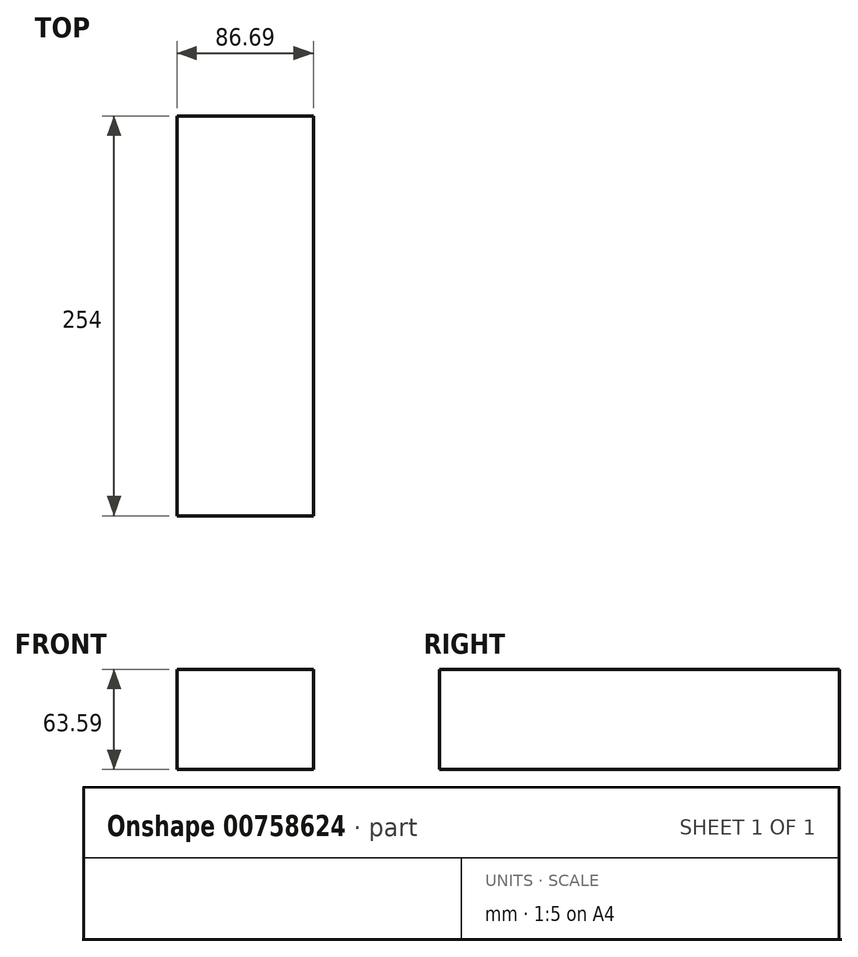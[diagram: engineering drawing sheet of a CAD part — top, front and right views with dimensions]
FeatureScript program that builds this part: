
annotation { "Feature Type Name" : "Feature", "Feature Type Description" : "" }
export const myFeature = defineFeature(function(context is Context, id is Id, definition is map)
    precondition{}
    {
        {
            var Q0;
            Q0=qCreatedBy(makeId("Front.planeOp"),FACE);
            var sketch = newSketch(context, id + "F0", { "sketchPlane" : qUnion([Q0])});
            skLineSegment(sketch, "E0.bottom", {"start": v(-30, 40.18) * mm, "end": v(56.7, 40.18) * mm});
            skLineSegment(sketch, "E0.top", {"start": v(-30, -23.4) * mm, "end": v(56.7, -23.4) * mm});
            skLineSegment(sketch, "E0.left", {"start": v(-30, 40.18) * mm, "end": v(-30, -23.4) * mm});
            skLineSegment(sketch, "E0.right", {"start": v(56.7, 40.18) * mm, "end": v(56.7, -23.4) * mm});
            skSolve(sketch);
        }
        {
            var Q0;
            Q0=makeQuery(id+"F0.imprint","IMPRINT",FACE,{"disambiguationData":[TD([[makeQuery(id+"F0.imprint","IMPRINT",EDGE,{"derivedFrom":sQuery(id+"F0.wireOp",EDGE,"E0.bottom")}),-1.0]])]});
            extrude(context, id + "F1", {"entities" : qUnion([Q0]), "depth" : 254 * mm, "offsetDistance" : 25.4 * mm});
        }
    });
